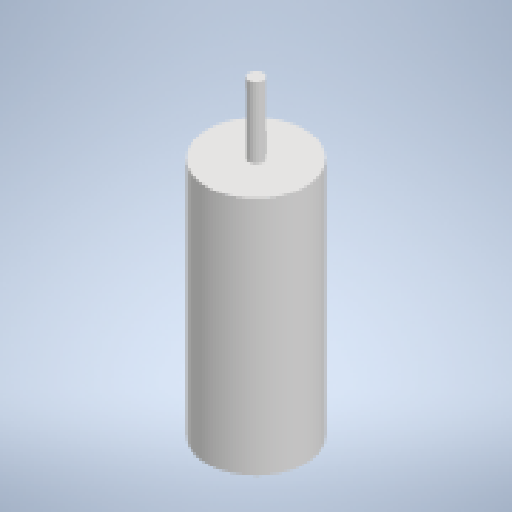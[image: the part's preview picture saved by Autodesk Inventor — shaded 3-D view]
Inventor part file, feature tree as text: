
AUTODESK INVENTOR PART (.ipt)
format: ipt  version: 2023.1 (Build 271208000, 208)  size: 236,032 bytes
history: native  units: mm
features: extrude x3, sketch x3
ambient origin geometry x8: Origin, YZ Plane, XZ Plane, XY Plane, X Axis, Y Axis, Z Axis, Center Point
bodies: Solid1 (feature_tree)
feature tree (6):
  extrude  "Extrusion1"  Depth=17.0mm TaperAngle=0.0deg
  extrude  "Extrusion2"  Depth=5.0mm TaperAngle=0.0deg
  extrude  "Extrusion3"  [1 undecoded]
  sketch  "Sketch1"  dims[d0=7.0mm d1=17.0mm d2=0.0mm]
  sketch  "Sketch2"  dims[d3=1.0mm d4=5.0mm d5=0.0mm]
  sketch  "Sketch3"  dims[d6=0.1mm d7=0.0mm]
note: 1 required parameter value undecoded (feature->parameter linkage not recoverable at this tier; creation-order binding heuristic only, values carry confidence <= 0.55)
